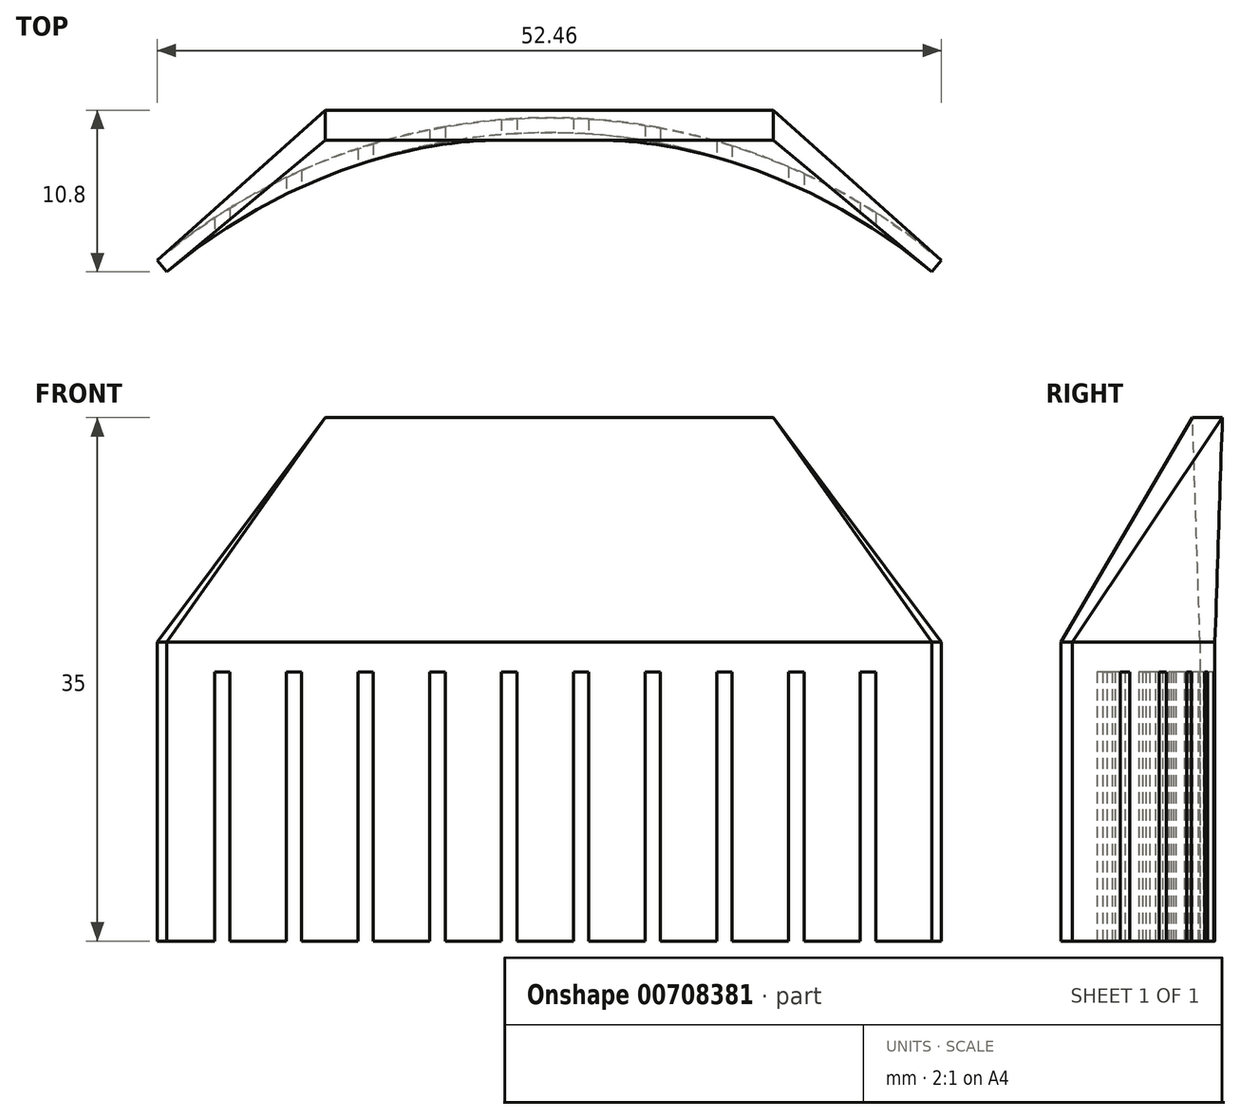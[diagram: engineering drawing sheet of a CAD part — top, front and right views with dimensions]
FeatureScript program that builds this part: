
annotation { "Feature Type Name" : "Feature", "Feature Type Description" : "" }
export const myFeature = defineFeature(function(context is Context, id is Id, definition is map)
    precondition{}
    {
        {
            var Q0;
            Q0=qCreatedBy(makeId("Top.planeOp"),FACE);
            var sketch = newSketch(context, id + "F0", { "sketchPlane" : qUnion([Q0])});
            skArc(sketch, "E0", {"start": v(25.59, 0) * mm, "mid": v(0, 9.3) * mm, "end": v(-25.59, 0) * mm});
            skArc(sketch, "E1.0", {"start": v(26.23, 0.77) * mm, "mid": v(0, 10.3) * mm, "end": v(-26.23, 0.77) * mm});
            skLineSegment(sketch, "E2", {"start": v(-25.59, 0) * mm, "end": v(-26.23, 0.77) * mm});
            skLineSegment(sketch, "E3", {"start": v(26.23, 0.77) * mm, "end": v(25.59, 0) * mm});
            skSolve(sketch);
        }
        {
            var Q0;
            Q0=makeQuery(id+"F0.imprint","IMPRINT",FACE,{"disambiguationData":[TD([[makeQuery(id+"F0.imprint","IMPRINT",EDGE,{"derivedFrom":sQuery(id+"F0.wireOp",EDGE,"E0")}),-1.0]])]});
            var Q1;
            Q1=sQuery(id+"F0.wireOp",EDGE,"E0");
            var Q2;
            Q2=sQuery(id+"F0.wireOp",EDGE,"E1.0");
            var Q3;
            Q3=sQuery(id+"F0.wireOp",EDGE,"E2");
            var Q4;
            Q4=sQuery(id+"F0.wireOp",EDGE,"E3");
            extrude(context, id + "F1", {"entities" : qUnion([Q0]), "surfaceEntities" : qUnion([Q1, Q2, Q3, Q4]), "depth" : 20 * mm, "offsetDistance" : 25 * mm});
        }
        {
            var Q0;
            Q0=qCreatedBy(makeId("Top.planeOp"),FACE);
            var sketch = newSketch(context, id + "F2", { "sketchPlane" : qUnion([Q0])});
            skLineSegment(sketch, "E4.bottom", {"start": v(-22.4, 13.1) * mm, "end": v(-21.36, 13.1) * mm});
            skLineSegment(sketch, "E4.top", {"start": v(-22.4, 0) * mm, "end": v(-21.36, 0) * mm});
            skLineSegment(sketch, "E4.left", {"start": v(-22.4, 13.1) * mm, "end": v(-22.4, 0) * mm});
            skLineSegment(sketch, "E4.right", {"start": v(-21.36, 13.1) * mm, "end": v(-21.36, 0) * mm});
            skLineSegment(sketch, "E5.1.0.0", {"start": v(-16.56, 13.1) * mm, "end": v(-16.56, 0) * mm});
            skLineSegment(sketch, "E5.1.0.1", {"start": v(-17.6, 13.1) * mm, "end": v(-17.6, 0) * mm});
            skLineSegment(sketch, "E5.1.0.2", {"start": v(-17.6, 0) * mm, "end": v(-16.56, 0) * mm});
            skLineSegment(sketch, "E5.1.0.3", {"start": v(-17.6, 13.1) * mm, "end": v(-16.56, 13.1) * mm});
            skLineSegment(sketch, "E5.2.0.0", {"start": v(-11.76, 13.1) * mm, "end": v(-11.76, 0) * mm});
            skLineSegment(sketch, "E5.2.0.1", {"start": v(-12.8, 13.1) * mm, "end": v(-12.8, 0) * mm});
            skLineSegment(sketch, "E5.2.0.2", {"start": v(-12.8, 0) * mm, "end": v(-11.76, 0) * mm});
            skLineSegment(sketch, "E5.2.0.3", {"start": v(-12.8, 13.1) * mm, "end": v(-11.76, 13.1) * mm});
            skLineSegment(sketch, "E5.3.0.0", {"start": v(-6.96, 13.1) * mm, "end": v(-6.96, 0) * mm});
            skLineSegment(sketch, "E5.3.0.1", {"start": v(-8, 13.1) * mm, "end": v(-8, 0) * mm});
            skLineSegment(sketch, "E5.3.0.2", {"start": v(-8, 0) * mm, "end": v(-6.96, 0) * mm});
            skLineSegment(sketch, "E5.3.0.3", {"start": v(-8, 13.1) * mm, "end": v(-6.96, 13.1) * mm});
            skLineSegment(sketch, "E5.4.0.0", {"start": v(-2.16, 13.1) * mm, "end": v(-2.16, 0) * mm});
            skLineSegment(sketch, "E5.4.0.1", {"start": v(-3.2, 13.1) * mm, "end": v(-3.2, 0) * mm});
            skLineSegment(sketch, "E5.4.0.2", {"start": v(-3.2, 0) * mm, "end": v(-2.16, 0) * mm});
            skLineSegment(sketch, "E5.4.0.3", {"start": v(-3.2, 13.1) * mm, "end": v(-2.16, 13.1) * mm});
            skLineSegment(sketch, "E5.5.0.0", {"start": v(2.64, 13.1) * mm, "end": v(2.64, 0) * mm});
            skLineSegment(sketch, "E5.5.0.1", {"start": v(1.6, 13.1) * mm, "end": v(1.6, 0) * mm});
            skLineSegment(sketch, "E5.5.0.2", {"start": v(1.6, 0) * mm, "end": v(2.64, 0) * mm});
            skLineSegment(sketch, "E5.5.0.3", {"start": v(1.6, 13.1) * mm, "end": v(2.64, 13.1) * mm});
            skLineSegment(sketch, "E5.6.0.0", {"start": v(7.44, 13.1) * mm, "end": v(7.44, 0) * mm});
            skLineSegment(sketch, "E5.6.0.1", {"start": v(6.4, 13.1) * mm, "end": v(6.4, 0) * mm});
            skLineSegment(sketch, "E5.6.0.2", {"start": v(6.4, 0) * mm, "end": v(7.44, 0) * mm});
            skLineSegment(sketch, "E5.6.0.3", {"start": v(6.4, 13.1) * mm, "end": v(7.44, 13.1) * mm});
            skLineSegment(sketch, "E5.7.0.0", {"start": v(12.24, 13.1) * mm, "end": v(12.24, 0) * mm});
            skLineSegment(sketch, "E5.7.0.1", {"start": v(11.2, 13.1) * mm, "end": v(11.2, 0) * mm});
            skLineSegment(sketch, "E5.7.0.2", {"start": v(11.2, 0) * mm, "end": v(12.24, 0) * mm});
            skLineSegment(sketch, "E5.7.0.3", {"start": v(11.2, 13.1) * mm, "end": v(12.24, 13.1) * mm});
            skLineSegment(sketch, "E5.8.0.0", {"start": v(17.04, 13.1) * mm, "end": v(17.04, 0) * mm});
            skLineSegment(sketch, "E5.8.0.1", {"start": v(16, 13.1) * mm, "end": v(16, 0) * mm});
            skLineSegment(sketch, "E5.8.0.2", {"start": v(16, 0) * mm, "end": v(17.04, 0) * mm});
            skLineSegment(sketch, "E5.8.0.3", {"start": v(16, 13.1) * mm, "end": v(17.04, 13.1) * mm});
            skLineSegment(sketch, "E5.9.0.0", {"start": v(21.84, 13.1) * mm, "end": v(21.84, 0) * mm});
            skLineSegment(sketch, "E5.9.0.1", {"start": v(20.8, 13.1) * mm, "end": v(20.8, 0) * mm});
            skLineSegment(sketch, "E5.9.0.2", {"start": v(20.8, 0) * mm, "end": v(21.84, 0) * mm});
            skLineSegment(sketch, "E5.9.0.3", {"start": v(20.8, 13.1) * mm, "end": v(21.84, 13.1) * mm});
            skLineSegment(sketch, "E5.direction1", {"start": v(-22.4, 0) * mm, "end": v(-17.6, 0) * mm, "construction": true});
            skSolve(sketch);
        }
        {
            var Q0;
            Q0 = qSketchRegion(id + "F2", true);
            extrude(context, id + "F3", {"entities" : qUnion([Q0]), "operationType" : NewBodyOperationType.REMOVE, "depth" : 18 * mm, "offsetDistance" : 25 * mm});
        }
        {
            var Q0;
            Q0=qCreatedBy(makeId("Top.planeOp"),FACE);
            cPlane(context, id + "F4", {"entities" : qUnion([Q0]), "cplaneType" : CPlaneType.OFFSET, "offset" : 35 * mm, "width" : 150 * mm, "height" : 150 * mm});
        }
        {
            var Q0;
            Q0=qCreatedBy(id+"F4.planeOp",FACE);
            var sketch = newSketch(context, id + "F5", { "sketchPlane" : qUnion([Q0])});
            skLineSegment(sketch, "E6.bottom", {"start": v(15, 10.8) * mm, "end": v(-15, 10.8) * mm});
            skLineSegment(sketch, "E6.top", {"start": v(15, 8.8) * mm, "end": v(-15, 8.8) * mm});
            skLineSegment(sketch, "E6.left", {"start": v(15, 10.8) * mm, "end": v(15, 8.8) * mm});
            skLineSegment(sketch, "E6.right", {"start": v(-15, 10.8) * mm, "end": v(-15, 8.8) * mm});
            skSolve(sketch);
        }
        {
            var Q1;
            Q1=makeQuery(id+"F1.opExtrude","CAP_FACE",FACE,{"disambiguationData":[OSD([sQuery(id+"F0.wireOp",EDGE,"E0"),sQuery(id+"F0.wireOp",EDGE,"E1.0"),sQuery(id+"F0.wireOp",EDGE,"E2"),sQuery(id+"F0.wireOp",EDGE,"E3")])],"isStart":false});
            var Q2;
            Q2=makeQuery(id+"F5.imprint","IMPRINT",FACE,{"disambiguationData":[TD([[makeQuery(id+"F5.imprint","IMPRINT",EDGE,{"derivedFrom":sQuery(id+"F5.wireOp",EDGE,"E6.bottom")}),1.0]])]});
            loft(context, id + "F6", {"operationType" : NewBodyOperationType.ADD, "sheetProfilesArray" : [{ "sheetProfileEntities" : qUnion([Q1]) }, { "sheetProfileEntities" : qUnion([Q2]) }]});
        }
    });
